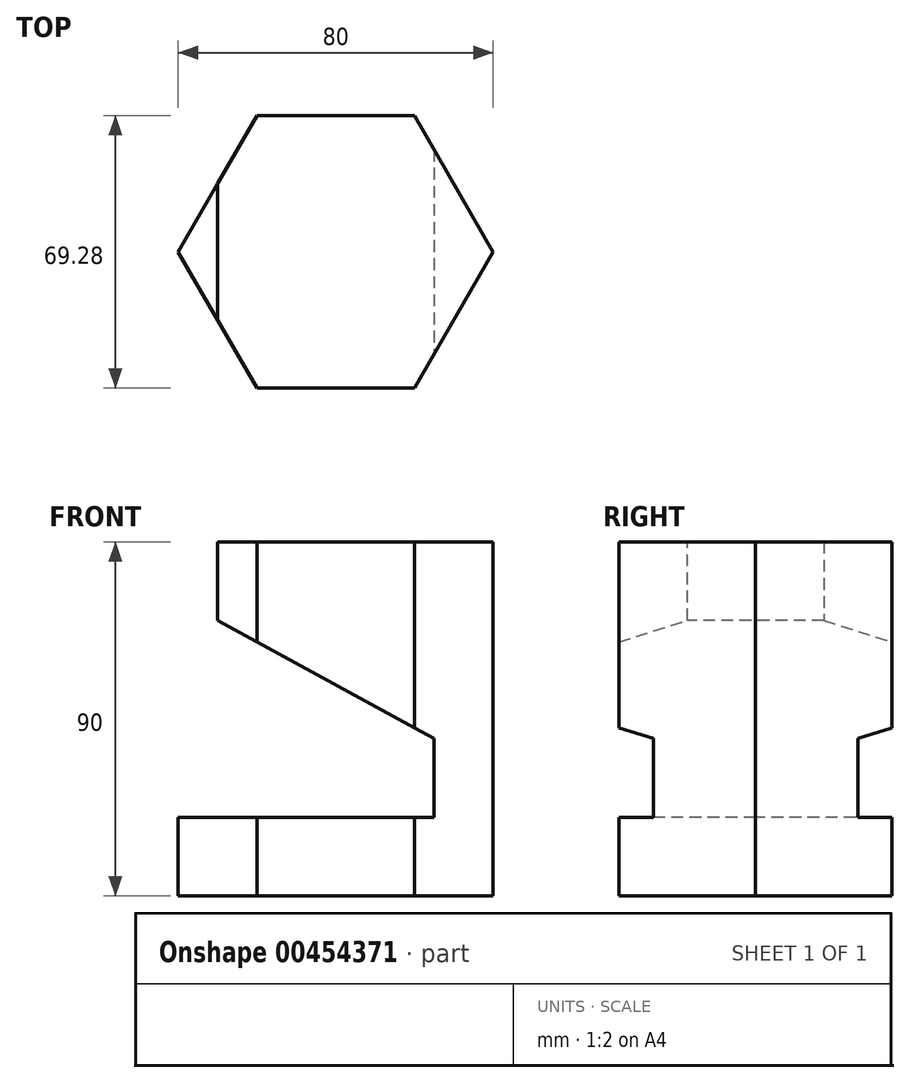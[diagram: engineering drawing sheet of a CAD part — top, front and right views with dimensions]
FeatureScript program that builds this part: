
annotation { "Feature Type Name" : "Feature", "Feature Type Description" : "" }
export const myFeature = defineFeature(function(context is Context, id is Id, definition is map)
    precondition{}
    {
        {
            var Q0;
            Q0=qCreatedBy(makeId("Top.planeOp"),FACE);
            var sketch = newSketch(context, id + "F0", { "sketchPlane" : qUnion([Q0])});
            skCircle(sketch, "E0", {"center": v(0, 0) * mm, "radius": 40 * mm, "construction": true});
            skLineSegment(sketch, "E1", {"start": v(-40, 0) * mm, "end": v(-20, 34.64) * mm});
            skLineSegment(sketch, "E2", {"start": v(-20, 34.64) * mm, "end": v(20, 34.64) * mm});
            skLineSegment(sketch, "E3", {"start": v(20, 34.64) * mm, "end": v(40, 0) * mm});
            skLineSegment(sketch, "E4", {"start": v(40, 0) * mm, "end": v(20, -34.64) * mm});
            skLineSegment(sketch, "E5", {"start": v(20, -34.64) * mm, "end": v(-20, -34.64) * mm});
            skLineSegment(sketch, "E6", {"start": v(-20, -34.64) * mm, "end": v(-40, 0) * mm});
            skSolve(sketch);
        }
        {
            var Q0;
            Q0=makeQuery(id+"F0.imprint","IMPRINT",FACE,{"disambiguationData":[TD([[makeQuery(id+"F0.imprint","IMPRINT",EDGE,{"derivedFrom":sQuery(id+"F0.wireOp",EDGE,"E1")}),-1.0]])]});
            extrude(context, id + "F1", {"entities" : qUnion([Q0]), "depth" : 90 * mm});
        }
        {
            var Q0;
            Q0=qCreatedBy(makeId("Front.planeOp"),FACE);
            var sketch = newSketch(context, id + "F2", { "sketchPlane" : qUnion([Q0])});
            skLineSegment(sketch, "E7", {"start": v(-43.14, 20) * mm, "end": v(25, 20) * mm});
            skLineSegment(sketch, "E8", {"start": v(25, 20) * mm, "end": v(25, 40) * mm});
            skLineSegment(sketch, "E9", {"start": v(25, 40) * mm, "end": v(-30, 70) * mm});
            skLineSegment(sketch, "E10", {"start": v(-30, 70) * mm, "end": v(-30, 92.66) * mm});
            skLineSegment(sketch, "E11", {"start": v(-30, 92.66) * mm, "end": v(-43.14, 92.66) * mm});
            skLineSegment(sketch, "E12", {"start": v(-43.14, 92.66) * mm, "end": v(-43.14, 20) * mm});
            skSolve(sketch);
        }
        {
            var Q0;
            Q0=makeQuery(id+"F2.imprint","IMPRINT",FACE,{"disambiguationData":[TD([[makeQuery(id+"F2.imprint","IMPRINT",EDGE,{"derivedFrom":sQuery(id+"F2.wireOp",EDGE,"E7")}),1.0]])]});
            extrude(context, id + "F3", {"entities" : qUnion([Q0]), "operationType" : NewBodyOperationType.REMOVE, "endBound" : BoundingType.THROUGH_ALL, "oppositeDirection" : true, "depth" : 25 * mm, "hasSecondDirection" : true, "secondDirectionBound" : SecondDirectionBoundingType.THROUGH_ALL, "secondDirectionOppositeDirection" : false, "secondDirectionDepth" : 25 * mm});
        }
    });
